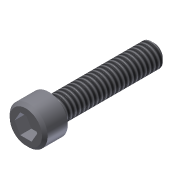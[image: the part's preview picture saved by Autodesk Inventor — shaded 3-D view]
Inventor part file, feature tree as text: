
AUTODESK INVENTOR PART (.ipt)
format: ipt  version: 2013 (Build 170138000, 138)  size: 107,520 bytes
history: native  units: in
note: dims shown in document units (in); Inventor stores cm internally (conversion verified against a paired STEP export)
features: extrude x3, sketch x3, chamfer x2, thread x1
ambient origin geometry x8: Origin, YZ Plane, XZ Plane, XY Plane, X Axis, Y Axis, Z Axis, Center Point
bodies: Solid1 (feature_tree)
feature tree (9):
  extrude  "Extrusion1"  Depth=0.164in TaperAngle=0.0deg
  extrude  "Extrusion2"  Depth=0.75in TaperAngle=0.0deg
  extrude  "Extrusion3"  Depth=0.08in TaperAngle=0.0deg
  thread  "Thread1"  [1 undecoded]
  chamfer  "Chamfer1"  [1 undecoded]
  chamfer  "Chamfer2"  [1 undecoded]
  sketch  "Sketch1"  dims[d0=0.27in d1=0.164in d2=0.0in]
  sketch  "Sketch2"  dims[d3=0.164in d4=0.75in d5=0.0in]
  sketch  "Sketch3"  dims[d6=0.1406in d7=0.08in d8=0.0in d9=1.0in d10=0.0in d11=0.02in d12=0.125in d13=45.0deg d14=0.02in d15=0.125in d16=45.0deg]
note: 3 required parameter values undecoded (feature->parameter linkage not recoverable at this tier; creation-order binding heuristic only, values carry confidence <= 0.55)
